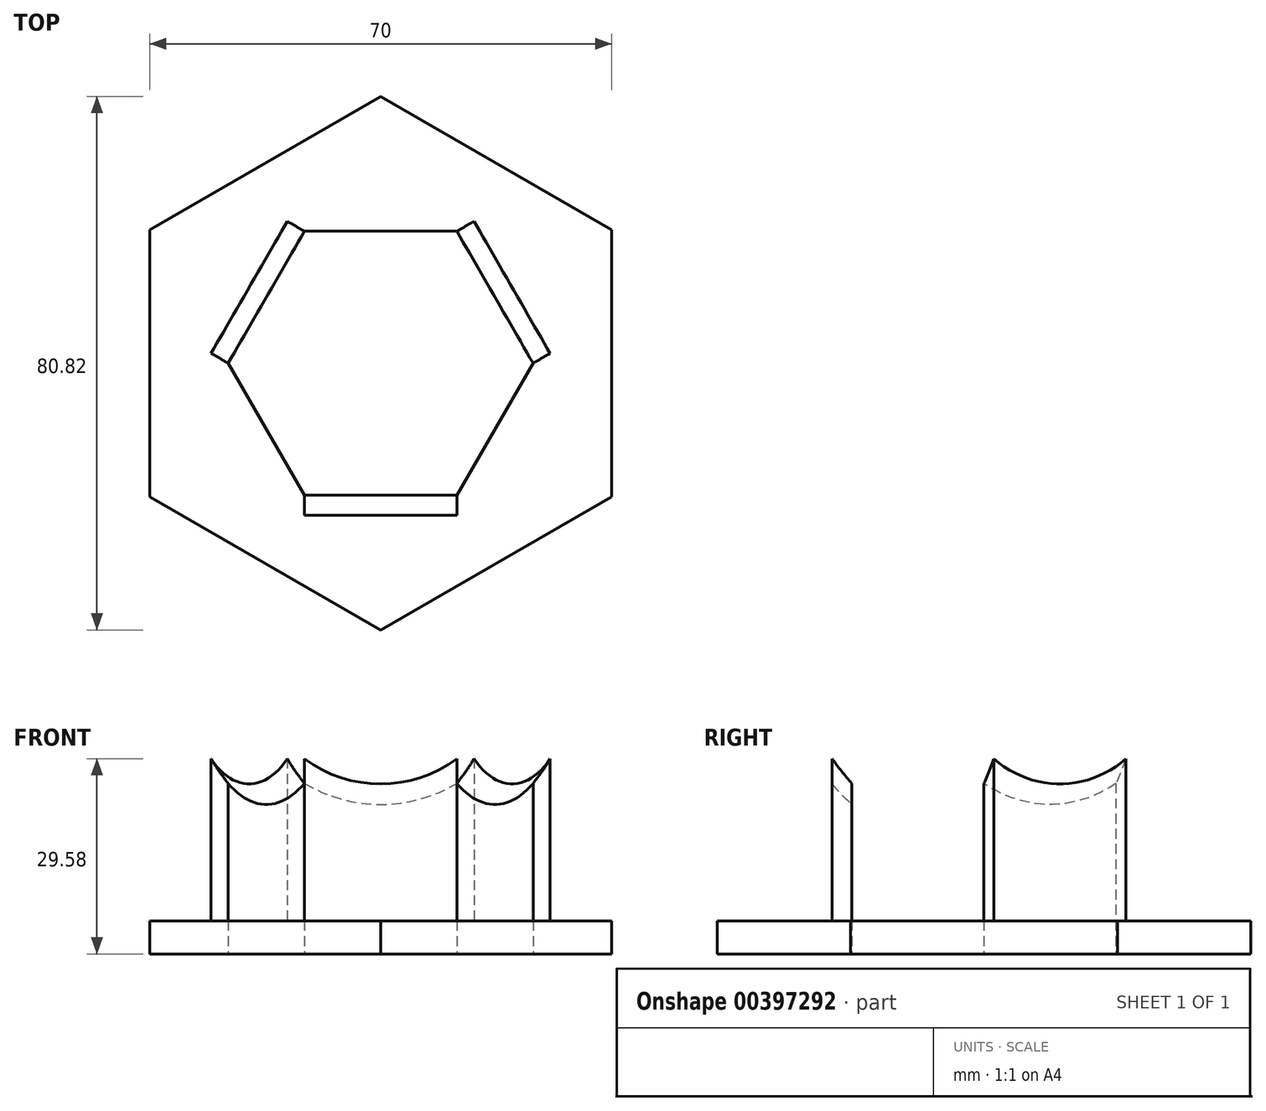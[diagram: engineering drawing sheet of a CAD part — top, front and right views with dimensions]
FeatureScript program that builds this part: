
annotation { "Feature Type Name" : "Feature", "Feature Type Description" : "" }
export const myFeature = defineFeature(function(context is Context, id is Id, definition is map)
    precondition{}
    {
        {
            var Q0;
            Q0=qCreatedBy(makeId("Top.planeOp"),FACE);
            var sketch = newSketch(context, id + "F0", { "sketchPlane" : qUnion([Q0])});
            skCircle(sketch, "E0.cCircle", {"center": v(0, 0) * mm, "radius": 35 * mm, "construction": true});
            skLineSegment(sketch, "E0.0", {"start": v(35, 20.2) * mm, "end": v(35, -20.2) * mm});
            skLineSegment(sketch, "E0.1", {"start": v(35, -20.2) * mm, "end": v(0, -40.41) * mm});
            skLineSegment(sketch, "E0.2", {"start": v(0, -40.41) * mm, "end": v(-35, -20.2) * mm});
            skLineSegment(sketch, "E0.3", {"start": v(-35, -20.2) * mm, "end": v(-35, 20.2) * mm});
            skLineSegment(sketch, "E0.4", {"start": v(-35, 20.2) * mm, "end": v(0, 40.41) * mm});
            skLineSegment(sketch, "E0.5", {"start": v(0, 40.41) * mm, "end": v(35, 20.2) * mm});
            skPoint(sketch, "E0.0.midPoint", {"position": v(35, 0) * mm});
            skCircle(sketch, "E1.cCircle", {"center": v(0, 0) * mm, "radius": 20 * mm, "construction": true});
            skLineSegment(sketch, "E1.0", {"start": v(-11.55, 20) * mm, "end": v(11.55, 20) * mm});
            skLineSegment(sketch, "E1.1", {"start": v(11.55, 20) * mm, "end": v(23.1, 0) * mm});
            skLineSegment(sketch, "E1.2", {"start": v(23.1, 0) * mm, "end": v(11.55, -20) * mm});
            skLineSegment(sketch, "E1.3", {"start": v(11.55, -20) * mm, "end": v(-11.55, -20) * mm});
            skLineSegment(sketch, "E1.4", {"start": v(-11.55, -20) * mm, "end": v(-23.1, 0) * mm});
            skLineSegment(sketch, "E1.5", {"start": v(-23.1, 0) * mm, "end": v(-11.55, 20) * mm});
            skPoint(sketch, "E1.0.midPoint", {"position": v(0, 20) * mm});
            skSolve(sketch);
        }
        {
            var Q0;
            Q0=makeQuery(id+"F0.imprint","IMPRINT",FACE,{"disambiguationData":[TD([[makeQuery(id+"F0.imprint","IMPRINT",EDGE,{"derivedFrom":sQuery(id+"F0.wireOp",EDGE,"E0.0")}),-1.0]])]});
            extrude(context, id + "F1", {"entities" : qUnion([Q0]), "depth" : 5 * mm});
        }
        {
            var Q0;
            Q0=makeQuery(id+"F1.opExtrude","CAP_FACE",FACE,{"disambiguationData":[OSD([sQuery(id+"F0.wireOp",EDGE,"E0.0"),sQuery(id+"F0.wireOp",EDGE,"E0.1"),sQuery(id+"F0.wireOp",EDGE,"E0.2"),sQuery(id+"F0.wireOp",EDGE,"E0.3"),sQuery(id+"F0.wireOp",EDGE,"E0.4"),sQuery(id+"F0.wireOp",EDGE,"E0.5"),sQuery(id+"F0.wireOp",EDGE,"E1.0"),sQuery(id+"F0.wireOp",EDGE,"E1.1"),sQuery(id+"F0.wireOp",EDGE,"E1.2"),sQuery(id+"F0.wireOp",EDGE,"E1.3"),sQuery(id+"F0.wireOp",EDGE,"E1.4"),sQuery(id+"F0.wireOp",EDGE,"E1.5")])],"isStart":false});
            var sketch = newSketch(context, id + "F2", { "sketchPlane" : qUnion([Q0])});
            skLineSegment(sketch, "E2", {"start": v(-11.55, 20) * mm, "end": v(-14.15, 21.5) * mm});
            skLineSegment(sketch, "E3", {"start": v(-23.1, 0) * mm, "end": v(-25.7, 1.5) * mm});
            skLineSegment(sketch, "E4", {"start": v(-14.15, 21.5) * mm, "end": v(-25.7, 1.5) * mm});
            skLineSegment(sketch, "E5", {"start": v(11.55, 20) * mm, "end": v(14.15, 21.5) * mm});
            skLineSegment(sketch, "E6", {"start": v(23.1, 0) * mm, "end": v(25.7, 1.5) * mm});
            skLineSegment(sketch, "E7", {"start": v(14.15, 21.5) * mm, "end": v(25.7, 1.5) * mm});
            skLineSegment(sketch, "E8", {"start": v(11.55, -20) * mm, "end": v(11.55, -23) * mm});
            skLineSegment(sketch, "E9", {"start": v(-11.55, -20) * mm, "end": v(-11.55, -23) * mm});
            skLineSegment(sketch, "E10", {"start": v(-11.55, -23) * mm, "end": v(11.55, -23) * mm});
            skSolve(sketch);
        }
        {
            var Q0;
            Q0 = qSketchRegion(id + "F2", true);
            var Q1;
            Q1=makeQuery(id+"F2.imprint","IMPRINT",FACE,{"disambiguationData":[TD([[makeQuery(id+"F2.imprint","IMPRINT",EDGE,{"derivedFrom":sQuery(id+"F2.wireOp",EDGE,"E2")}),1.0]])]});
            var Q2;
            Q2=makeQuery(id+"F2.imprint","IMPRINT",FACE,{"disambiguationData":[TD([[makeQuery(id+"F2.imprint","IMPRINT",EDGE,{"derivedFrom":sQuery(id+"F2.wireOp",EDGE,"E5")}),-1.0]])]});
            var Q3;
            Q3=makeQuery(id+"F2.imprint","IMPRINT",FACE,{"disambiguationData":[TD([[makeQuery(id+"F2.imprint","IMPRINT",EDGE,{"derivedFrom":sQuery(id+"F2.wireOp",EDGE,"E8")}),-1.0]])]});
            extrude(context, id + "F3", {"entities" : qUnion([Q0, Q1, Q2, Q3]), "operationType" : NewBodyOperationType.ADD, "depth" : 40 * mm});
        }
        {
            var Q0;
            Q0=makeQuery(id+"F3.opExtrude","CAP_FACE",FACE,{"disambiguationData":[OSD([sQuery(id+"F0.wireOp",EDGE,"E1.1"),sQuery(id+"F2.wireOp",EDGE,"E5"),sQuery(id+"F2.wireOp",EDGE,"E6"),sQuery(id+"F2.wireOp",EDGE,"E7")])],"isStart":false});
            var sketch = newSketch(context, id + "F4", { "sketchPlane" : qUnion([Q0])});
            skCircle(sketch, "E11", {"center": v(0, 0) * mm, "radius": 30 * mm});
            skLineSegment(sketch, "E12", {"start": v(0, 30) * mm, "end": v(0, -30) * mm});
            skSolve(sketch);
        }
        {
            var Q0;
            {var subQ0=sQuery(id+"F4.wireOp",EDGE,"E12");Q0=makeQuery(id+"F4.imprint","IMPRINT",FACE,{"disambiguationData":[TD([[makeQuery(id+"F4.imprint","IMPRINT",EDGE,{"derivedFrom":subQ0}),-1.0]])]});}
            var Q1;
            Q1=sQuery(id+"F4.wireOp",EDGE,"E12");
            revolve(context, id + "F5", {"operationType" : NewBodyOperationType.REMOVE, "entities" : qUnion([Q0]), "axis" : qUnion([Q1]), "revolveType" : RevolveType.FULL, "oppositeDirection" : true});
        }
    });
